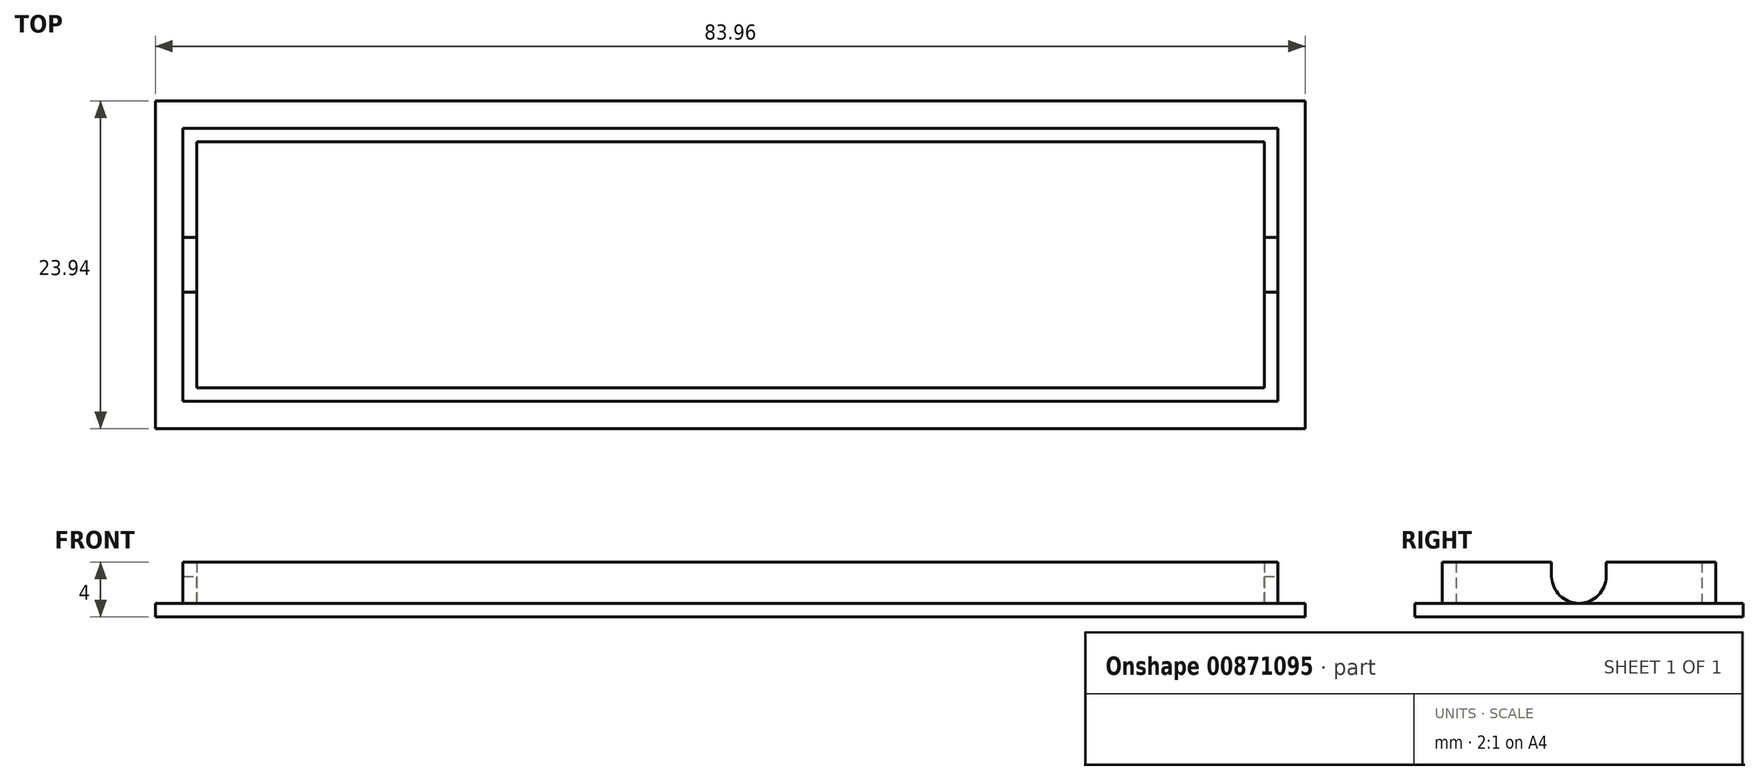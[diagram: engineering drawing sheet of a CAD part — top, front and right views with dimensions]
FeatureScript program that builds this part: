
annotation { "Feature Type Name" : "Feature", "Feature Type Description" : "" }
export const myFeature = defineFeature(function(context is Context, id is Id, definition is map)
    precondition{}
    {
        {
            var Q0;
            Q0=qCreatedBy(makeId("Top.planeOp"),FACE);
            var sketch = newSketch(context, id + "F0", { "sketchPlane" : qUnion([Q0])});
            skLineSegment(sketch, "E0.bottom", {"start": v(39.98, -9.97) * mm, "end": v(-39.98, -9.98) * mm});
            skLineSegment(sketch, "E0.top", {"start": v(39.98, 9.98) * mm, "end": v(-39.98, 9.97) * mm});
            skLineSegment(sketch, "E0.left", {"start": v(39.98, -9.97) * mm, "end": v(39.98, 9.98) * mm});
            skLineSegment(sketch, "E0.right", {"start": v(-39.98, -9.98) * mm, "end": v(-39.98, 9.97) * mm});
            skPoint(sketch, "E0.middle", {"position": v(0, 0) * mm});
            skLineSegment(sketch, "E1.0", {"start": v(41.98, 11.98) * mm, "end": v(-41.98, 11.97) * mm});
            skLineSegment(sketch, "E1.1", {"start": v(41.98, -11.97) * mm, "end": v(41.98, 11.98) * mm});
            skLineSegment(sketch, "E1.2", {"start": v(41.98, -11.97) * mm, "end": v(-41.98, -11.98) * mm});
            skLineSegment(sketch, "E1.3", {"start": v(-41.98, -11.98) * mm, "end": v(-41.98, 11.97) * mm});
            skLineSegment(sketch, "E2.0", {"start": v(38.98, 8.98) * mm, "end": v(-38.98, 8.97) * mm});
            skLineSegment(sketch, "E2.1", {"start": v(38.98, -8.97) * mm, "end": v(38.98, 8.98) * mm});
            skLineSegment(sketch, "E2.2", {"start": v(38.98, -8.97) * mm, "end": v(-38.98, -8.98) * mm});
            skLineSegment(sketch, "E2.3", {"start": v(-38.98, -8.98) * mm, "end": v(-38.98, 8.97) * mm});
            skSolve(sketch);
        }
        {
            var Q0;
            Q0=makeQuery(id+"F0.imprint","IMPRINT",FACE,{"disambiguationData":[TD([[makeQuery(id+"F0.imprint","IMPRINT",EDGE,{"derivedFrom":sQuery(id+"F0.wireOp",EDGE,"E0.bottom")}),-1.0]])]});
            extrude(context, id + "F1", {"entities" : qUnion([Q0]), "depth" : 4 * mm, "offsetDistance" : 25 * mm});
        }
        {
            var Q0;
            Q0=makeQuery(id+"F0.imprint","IMPRINT",FACE,{"disambiguationData":[TD([[makeQuery(id+"F0.imprint","IMPRINT",EDGE,{"derivedFrom":sQuery(id+"F0.wireOp",EDGE,"E0.bottom")}),1.0]])]});
            var Q1;
            Q1=makeQuery(id+"F0.imprint","IMPRINT",FACE,{"disambiguationData":[TD([[makeQuery(id+"F0.imprint","IMPRINT",EDGE,{"derivedFrom":sQuery(id+"F0.wireOp",EDGE,"E2.0")}),1.0]])]});
            extrude(context, id + "F2", {"entities" : qUnion([Q0, Q1]), "operationType" : NewBodyOperationType.ADD, "depth" : 1 * mm, "offsetDistance" : 25 * mm});
        }
        {
            var Q0;
            Q0=makeQuery(id+"F1.opExtrude","SWEPT_FACE",FACE,{"disambiguationData":[OSD([sQuery(id+"F0.wireOp",EDGE,"E0.left")])]});
            var sketch = newSketch(context, id + "F3", { "sketchPlane" : qUnion([Q0])});
            skArc(sketch, "E3", {"start": v(-2, 3.04) * mm, "mid": v(0, 1) * mm, "end": v(2, 3.04) * mm});
            skLineSegment(sketch, "E4", {"start": v(-2, 2.96) * mm, "end": v(-2, 4) * mm});
            skLineSegment(sketch, "E5", {"start": v(2, 2.96) * mm, "end": v(2, 4) * mm});
            skLineSegment(sketch, "E6", {"start": v(-2, 4) * mm, "end": v(2, 4) * mm});
            skSolve(sketch);
        }
        {
            var Q0;
            {var subQ3=sQuery(id+"F3.wireOp",EDGE,"E6");Q0=makeQuery(id+"F3.imprint","IMPRINT",FACE,{"disambiguationData":[TD([[makeQuery(id+"F3.imprint","IMPRINT",EDGE,{"derivedFrom":subQ3}),-1.0]])]});}
            extrude(context, id + "F4", {"entities" : qUnion([Q0]), "operationType" : NewBodyOperationType.REMOVE, "oppositeDirection" : true, "depth" : 100 * mm, "offsetDistance" : 25 * mm});
        }
    });
